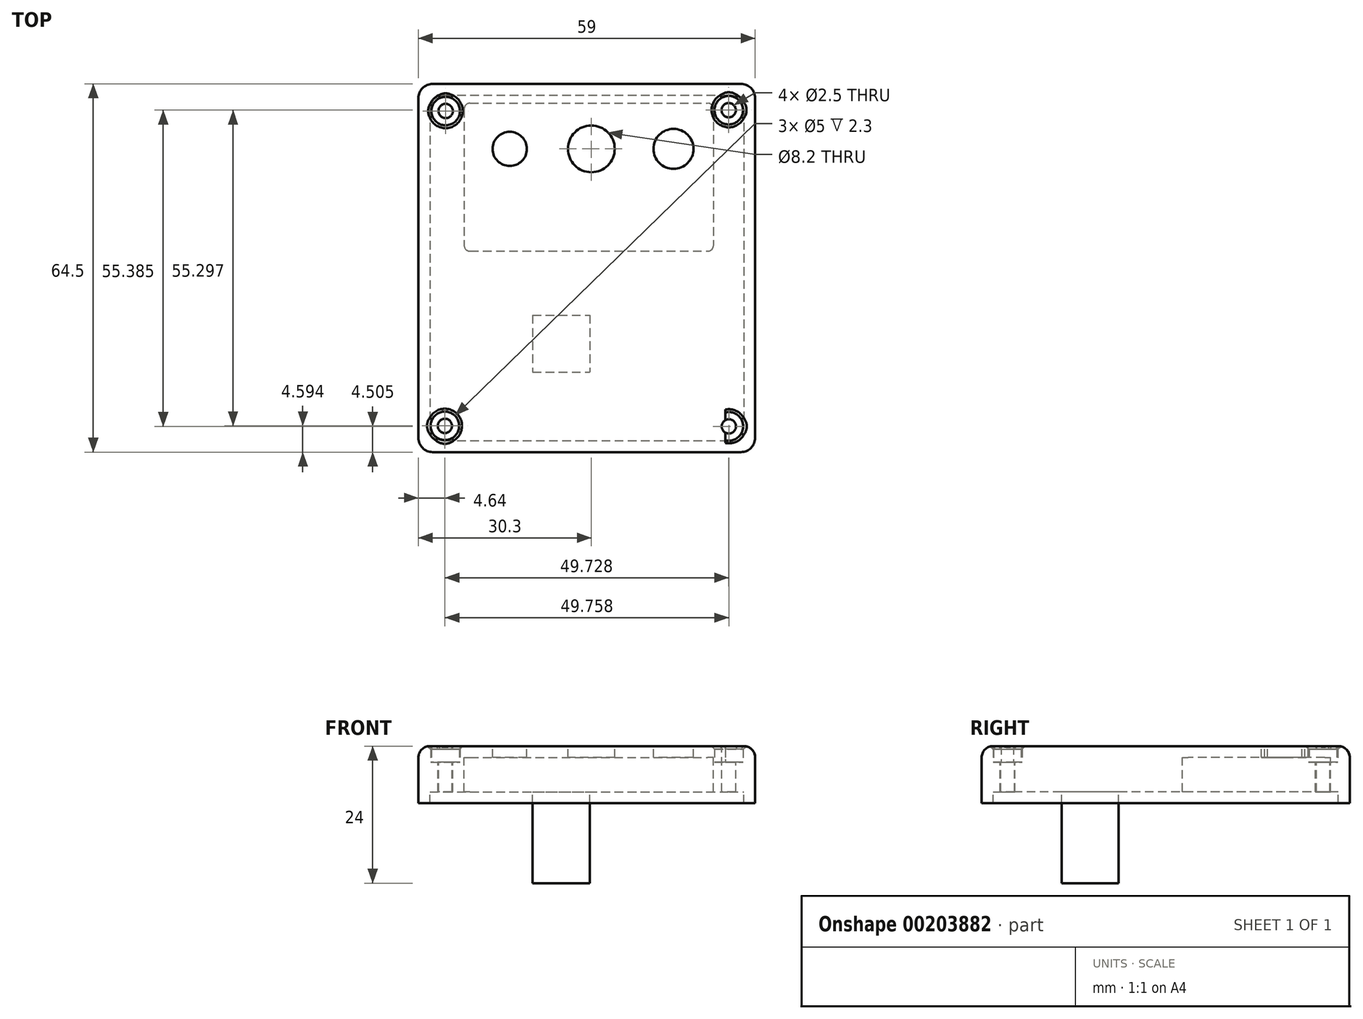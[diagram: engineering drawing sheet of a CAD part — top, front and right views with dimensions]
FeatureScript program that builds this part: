
annotation { "Feature Type Name" : "Feature", "Feature Type Description" : "" }
export const myFeature = defineFeature(function(context is Context, id is Id, definition is map)
    precondition{}
    {
        {
            var Q0;
            Q0=qCreatedBy(makeId("Top.planeOp"),FACE);
            var sketch = newSketch(context, id + "F0", { "sketchPlane" : qUnion([Q0])});
            skLineSegment(sketch, "E0.bottom", {"start": v(-36.58, 47.75) * mm, "end": v(22.42, 47.75) * mm});
            skLineSegment(sketch, "E0.top", {"start": v(-36.58, -16.75) * mm, "end": v(22.42, -16.75) * mm});
            skLineSegment(sketch, "E0.left", {"start": v(-36.58, 47.75) * mm, "end": v(-36.58, -16.75) * mm});
            skLineSegment(sketch, "E0.right", {"start": v(22.42, 47.75) * mm, "end": v(22.42, -16.75) * mm});
            skLineSegment(sketch, "E1.bottom", {"start": v(-34.58, 45.75) * mm, "end": v(20.42, 45.75) * mm});
            skLineSegment(sketch, "E1.top", {"start": v(-34.58, -14.75) * mm, "end": v(20.42, -14.75) * mm});
            skLineSegment(sketch, "E1.left", {"start": v(-34.58, 45.75) * mm, "end": v(-34.58, -14.75) * mm});
            skLineSegment(sketch, "E1.right", {"start": v(20.42, 45.75) * mm, "end": v(20.42, -14.75) * mm});
            skLineSegment(sketch, "E2.right", {"start": v(-34.58, -2) * mm, "end": v(-34.58, 2) * mm});
            skLineSegment(sketch, "E3.bottom", {"start": v(-34.58, 45.75) * mm, "end": v(9.72, 45.75) * mm});
            skLineSegment(sketch, "E4.top", {"start": v(-34.58, -14.75) * mm, "end": v(-32.58, -14.75) * mm});
            skLineSegment(sketch, "E4.left", {"start": v(-34.58, -8.75) * mm, "end": v(-34.58, -14.75) * mm});
            skLineSegment(sketch, "E5.bottom", {"start": v(13.36, 45.75) * mm, "end": v(14.86, 45.75) * mm});
            skLineSegment(sketch, "E6.top", {"start": v(16.3, -14.75) * mm, "end": v(14.92, -14.75) * mm});
            skLineSegment(sketch, "E7.bottom", {"start": v(17.21, 9.77) * mm, "end": v(11.21, 9.77) * mm});
            skLineSegment(sketch, "E7.top", {"start": v(17.21, 4.77) * mm, "end": v(11.21, 4.77) * mm});
            skLineSegment(sketch, "E7.left", {"start": v(17.21, 9.77) * mm, "end": v(17.21, 4.77) * mm});
            skLineSegment(sketch, "E7.right", {"start": v(11.21, 9.77) * mm, "end": v(11.21, 4.77) * mm});
            skCircle(sketch, "E8", {"center": v(-31.94, -12.16) * mm, "radius": 1.25 * mm});
            skCircle(sketch, "E9", {"center": v(-31.8, 43) * mm, "radius": 2.5 * mm});
            skCircle(sketch, "E10", {"center": v(-31.8, 43) * mm, "radius": 1.25 * mm});
            skLineSegment(sketch, "E11", {"start": v(-29.3, 43) * mm, "end": v(-29.3, 45.75) * mm});
            skLineSegment(sketch, "E12.bottom", {"start": v(17.22, 16.75) * mm, "end": v(-34.58, 16.75) * mm});
            skLineSegment(sketch, "E12.top", {"start": v(17.22, 15.25) * mm, "end": v(-34.58, 15.25) * mm});
            skLineSegment(sketch, "E12.left", {"start": v(17.22, 15.25) * mm, "end": v(17.22, 16.75) * mm});
            skLineSegment(sketch, "E12.right", {"start": v(-34.58, 15.25) * mm, "end": v(-34.58, 16.75) * mm});
            skLineSegment(sketch, "E13.bottom", {"start": v(-34.58, 14.63) * mm, "end": v(-32.58, 14.63) * mm});
            skLineSegment(sketch, "E13.top", {"start": v(-34.58, 8.63) * mm, "end": v(-32.58, 8.63) * mm});
            skLineSegment(sketch, "E13.left", {"start": v(-34.58, 14.63) * mm, "end": v(-34.58, 8.63) * mm});
            skLineSegment(sketch, "E13.right", {"start": v(-32.58, 14.63) * mm, "end": v(-32.58, 8.63) * mm});
            skCircle(sketch, "E14", {"center": v(17.79, 43.14) * mm, "radius": 2.5 * mm});
            skCircle(sketch, "E15", {"center": v(17.79, 43.14) * mm, "radius": 1.25 * mm});
            skLineSegment(sketch, "E16", {"start": v(17.79, 40.64) * mm, "end": v(20.42, 40.64) * mm});
            skCircle(sketch, "E17", {"center": v(17.82, -12.24) * mm, "radius": 2.5 * mm});
            skCircle(sketch, "E18", {"center": v(17.82, -12.24) * mm, "radius": 1.25 * mm});
            skLineSegment(sketch, "E19", {"start": v(17.82, -9.74) * mm, "end": v(20.42, -9.74) * mm});
            skLineSegment(sketch, "E20.bottom", {"start": v(14.92, -14.75) * mm, "end": v(13.15, -14.75) * mm});
            skLineSegment(sketch, "E20.top", {"start": v(14.92, -13.29) * mm, "end": v(13.15, -13.29) * mm});
            skLineSegment(sketch, "E20.left", {"start": v(14.92, -14.75) * mm, "end": v(14.92, -13.29) * mm});
            skLineSegment(sketch, "E20.right", {"start": v(13.15, -14.75) * mm, "end": v(13.15, -13.29) * mm});
            skLineSegment(sketch, "E21", {"start": v(17.22, 45.75) * mm, "end": v(17.22, -14.75) * mm});
            skLineSegment(sketch, "E22", {"start": v(20.42, -9.02) * mm, "end": v(17.22, -9.02) * mm});
            skLineSegment(sketch, "E23.top", {"start": v(14.92, -7.79) * mm, "end": v(13.15, -7.79) * mm});
            skLineSegment(sketch, "E23.left", {"start": v(14.92, -13.29) * mm, "end": v(14.92, -7.79) * mm});
            skLineSegment(sketch, "E23.right", {"start": v(13.15, -13.29) * mm, "end": v(13.15, -7.79) * mm});
            skLineSegment(sketch, "E24", {"start": v(15.29, 43.14) * mm, "end": v(15.29, 45.75) * mm});
            skLineSegment(sketch, "E25", {"start": v(15.32, -12.24) * mm, "end": v(15.32, -14.75) * mm});
            skLineSegment(sketch, "E26.bottom", {"start": v(-19.58, -1.75) * mm, "end": v(5.42, -1.75) * mm});
            skLineSegment(sketch, "E26.top", {"start": v(-19.58, 7.25) * mm, "end": v(5.42, 7.25) * mm});
            skLineSegment(sketch, "E26.left", {"start": v(-19.58, -1.75) * mm, "end": v(-19.58, 7.25) * mm});
            skLineSegment(sketch, "E26.right", {"start": v(5.42, -1.75) * mm, "end": v(5.42, 7.25) * mm});
            skCircle(sketch, "E27", {"center": v(8.11, 36.36) * mm, "radius": 3.5 * mm});
            skLineSegment(sketch, "E28", {"start": v(-29.58, 15.25) * mm, "end": v(-29.58, -14.75) * mm, "construction": true});
            skLineSegment(sketch, "E29", {"start": v(17.22, 1.25) * mm, "end": v(-34.58, 1.25) * mm, "construction": true});
            skLineSegment(sketch, "E30", {"start": v(-34.58, 6.25) * mm, "end": v(17.21, 6.25) * mm, "construction": true});
            skLineSegment(sketch, "E31.right", {"start": v(8.3, -10.55) * mm, "end": v(8.3, -13.55) * mm});
            skCircle(sketch, "E32", {"center": v(-31.94, -12.16) * mm, "radius": 2.5 * mm});
            skLineSegment(sketch, "E33.bottom", {"start": v(-28.56, 44.36) * mm, "end": v(15.11, 44.36) * mm});
            skLineSegment(sketch, "E33.top", {"start": v(-28.56, 18.44) * mm, "end": v(15.11, 18.44) * mm});
            skLineSegment(sketch, "E33.left", {"start": v(-28.56, 44.36) * mm, "end": v(-28.56, 18.44) * mm});
            skLineSegment(sketch, "E33.right", {"start": v(15.11, 44.36) * mm, "end": v(15.11, 18.44) * mm});
            skLineSegment(sketch, "E34", {"start": v(-31.8, 40.5) * mm, "end": v(-34.58, 40.5) * mm});
            skLineSegment(sketch, "E35.bottom", {"start": v(-20, -2.24) * mm, "end": v(5.9, -2.24) * mm});
            skLineSegment(sketch, "E35.top", {"start": v(-20, 7.67) * mm, "end": v(5.9, 7.67) * mm});
            skLineSegment(sketch, "E35.left", {"start": v(-20, -2.24) * mm, "end": v(-20, 7.67) * mm});
            skLineSegment(sketch, "E35.right", {"start": v(5.9, -2.24) * mm, "end": v(5.9, 7.67) * mm});
            skCircle(sketch, "E36", {"center": v(-20.58, 36.36) * mm, "radius": 3 * mm});
            skPoint(sketch, "E37.oppositeSnap0", {"position": v(13.15, -10.54) * mm});
            skLineSegment(sketch, "E37.bottom", {"start": v(8.3, -13.55) * mm, "end": v(12.3, -13.55) * mm});
            skLineSegment(sketch, "E37.top", {"start": v(8.3, -10.54) * mm, "end": v(12.3, -10.54) * mm});
            skLineSegment(sketch, "E37.left", {"start": v(8.3, -13.55) * mm, "end": v(8.3, -10.54) * mm});
            skLineSegment(sketch, "E37.right", {"start": v(12.3, -13.55) * mm, "end": v(12.3, -10.54) * mm});
            skLineSegment(sketch, "E38", {"start": v(12.3, -13.55) * mm, "end": v(12.3, 17.84) * mm, "construction": true});
            skLineSegment(sketch, "E39.bottom", {"start": v(12.3, 15.25) * mm, "end": v(8.3, 15.25) * mm});
            skLineSegment(sketch, "E39.top", {"start": v(12.3, 13.25) * mm, "end": v(8.3, 13.25) * mm});
            skLineSegment(sketch, "E39.left", {"start": v(12.3, 15.25) * mm, "end": v(12.3, 13.25) * mm});
            skLineSegment(sketch, "E39.right", {"start": v(8.3, 15.25) * mm, "end": v(8.3, 13.25) * mm});
            skLineSegment(sketch, "E40", {"start": v(-6.28, 41.9) * mm, "end": v(-6.28, 32.7) * mm, "construction": true});
            skLineSegment(sketch, "E41", {"start": v(8.11, 36.36) * mm, "end": v(-21.69, 36.36) * mm, "construction": true});
            skCircle(sketch, "E42", {"center": v(-6.28, 36.36) * mm, "radius": 4.1 * mm});
            skSolve(sketch);
        }
        {
            var Q0;
            Q0=qCreatedBy(makeId("Top.planeOp"),FACE);
            var sketch = newSketch(context, id + "F1", { "sketchPlane" : qUnion([Q0])});
            skLineSegment(sketch, "E43.bottom", {"start": v(-36.58, 47.75) * mm, "end": v(22.42, 47.75) * mm});
            skLineSegment(sketch, "E43.top", {"start": v(-36.58, -16.75) * mm, "end": v(22.42, -16.75) * mm});
            skLineSegment(sketch, "E43.left", {"start": v(-36.58, 47.75) * mm, "end": v(-36.58, -16.75) * mm});
            skLineSegment(sketch, "E43.right", {"start": v(22.42, 47.75) * mm, "end": v(22.42, -16.75) * mm});
            skLineSegment(sketch, "E44.bottom", {"start": v(-34.58, 45.75) * mm, "end": v(20.42, 45.75) * mm});
            skLineSegment(sketch, "E44.top", {"start": v(-34.58, -14.75) * mm, "end": v(20.42, -14.75) * mm});
            skLineSegment(sketch, "E44.left", {"start": v(-34.58, 45.75) * mm, "end": v(-34.58, -14.75) * mm});
            skLineSegment(sketch, "E44.right", {"start": v(20.42, 45.75) * mm, "end": v(20.42, -14.75) * mm});
            skSolve(sketch);
        }
        {
            var Q0;
            Q0=qCreatedBy(makeId("Top.planeOp"),FACE);
            var sketch = newSketch(context, id + "F2", { "sketchPlane" : qUnion([Q0])});
            skLineSegment(sketch, "E45.bottom", {"start": v(-32.68, -7.56) * mm, "end": v(-26.46, -7.56) * mm});
            skLineSegment(sketch, "E45.top", {"start": v(-32.68, 10.68) * mm, "end": v(-26.46, 10.68) * mm});
            skLineSegment(sketch, "E45.left", {"start": v(-32.68, -7.56) * mm, "end": v(-32.68, 10.68) * mm});
            skLineSegment(sketch, "E45.right", {"start": v(-26.46, -7.56) * mm, "end": v(-26.46, 10.68) * mm});
            skSolve(sketch);
        }
        {
            var Q0;
            Q0=qCreatedBy(makeId("Top.planeOp"),FACE);
            var sketch = newSketch(context, id + "F3", { "sketchPlane" : qUnion([Q0])});
            skLineSegment(sketch, "E46.bottom", {"start": v(-36.58, 47.75) * mm, "end": v(22.42, 47.75) * mm});
            skLineSegment(sketch, "E46.top", {"start": v(-36.58, -16.75) * mm, "end": v(22.42, -16.75) * mm});
            skLineSegment(sketch, "E46.left", {"start": v(-36.58, 47.75) * mm, "end": v(-36.58, -16.75) * mm});
            skLineSegment(sketch, "E46.right", {"start": v(22.42, 47.75) * mm, "end": v(22.42, -16.75) * mm});
            skLineSegment(sketch, "E47", {"start": v(-29.58, 14.75) * mm, "end": v(-29.58, -29.34) * mm, "construction": true});
            skLineSegment(sketch, "E48", {"start": v(20.42, -4.25) * mm, "end": v(-34.58, -4.25) * mm, "construction": true});
            skLineSegment(sketch, "E49", {"start": v(17.22, 1.75) * mm, "end": v(-34.58, 1.75) * mm, "construction": true});
            skLineSegment(sketch, "E50", {"start": v(-34.58, 7.75) * mm, "end": v(-24.59, 7.75) * mm, "construction": true});
            skCircle(sketch, "E51", {"center": v(-29.58, -4.25) * mm, "radius": 2 * mm});
            skCircle(sketch, "E52", {"center": v(-29.58, 1.75) * mm, "radius": 2 * mm});
            skCircle(sketch, "E53", {"center": v(-29.58, 7.75) * mm, "radius": 2 * mm});
            skCircle(sketch, "E54", {"center": v(-29.58, 7.75) * mm, "radius": 2.75 * mm});
            skCircle(sketch, "E55", {"center": v(-29.58, 1.75) * mm, "radius": 2.75 * mm});
            skCircle(sketch, "E56", {"center": v(-29.58, -4.25) * mm, "radius": 2.75 * mm});
            skSolve(sketch);
        }
        {
            var Q0;
            Q0=makeQuery(id+"F1.imprint","IMPRINT",FACE,{"disambiguationData":[TD([[makeQuery(id+"F1.imprint","IMPRINT",EDGE,{"derivedFrom":sQuery(id+"F1.wireOp",EDGE,"E44.bottom")}),-1.0]])]});
            extrude(context, id + "F4", {"entities" : qUnion([Q0]), "oppositeDirection" : true, "depth" : 8 * mm});
        }
        {
            var Q0;
            Q0=makeQuery(id+"F1.imprint","IMPRINT",FACE,{"disambiguationData":[TD([[makeQuery(id+"F1.imprint","IMPRINT",EDGE,{"derivedFrom":sQuery(id+"F1.wireOp",EDGE,"E43.bottom")}),-1.0]])]});
            extrude(context, id + "F5", {"entities" : qUnion([Q0]), "operationType" : NewBodyOperationType.ADD, "oppositeDirection" : true, "depth" : 10 * mm});
        }
        {
            var Q0;
            {var subQ0=sQuery(id+"F0.wireOp",EDGE,"E8");var subQ1=sQuery(id+"F0.wireOp",EDGE,"E4.right");var subQ2=makeQuery(id+"F0.imprint","INTERSECT",VERTEX,{"disambiguationData":[OD(0.0)],"derivedFrom":[subQ1,subQ0]});Q0=makeQuery(id+"F0.imprint","IMPRINT",FACE,{"disambiguationData":[TD([[makeQuery(id+"F0.imprint","IMPRINT",EDGE,{"disambiguationData":[TD([[subQ2,-1.0]])],"derivedFrom":subQ1}),1.0]])]});}
            var Q1;
            {var subQ0=sQuery(id+"F0.wireOp",EDGE,"E8");var subQ1=sQuery(id+"F0.wireOp",EDGE,"E4.right");var subQ2=makeQuery(id+"F0.imprint","INTERSECT",VERTEX,{"disambiguationData":[OD(0.0)],"derivedFrom":[subQ1,subQ0]});Q1=makeQuery(id+"F0.imprint","IMPRINT",FACE,{"disambiguationData":[TD([[makeQuery(id+"F0.imprint","IMPRINT",EDGE,{"disambiguationData":[TD([[subQ2,-1.0]])],"derivedFrom":subQ1}),-1.0]])]});}
            var Q2;
            Q2=makeQuery(id+"F0.imprint","IMPRINT",FACE,{"disambiguationData":[TD([[makeQuery(id+"F0.imprint","IMPRINT",EDGE,{"derivedFrom":sQuery(id+"F0.wireOp",EDGE,"E10")}),1.0]])]});
            var Q3;
            {var subQ0=sQuery(id+"F0.wireOp",EDGE,"E21");var subQ1=sQuery(id+"F0.wireOp",EDGE,"E18");var subQ2=makeQuery(id+"F0.imprint","INTERSECT",VERTEX,{"disambiguationData":[OD(0.0)],"derivedFrom":[subQ1,subQ0]});Q3=makeQuery(id+"F0.imprint","IMPRINT",FACE,{"disambiguationData":[TD([[makeQuery(id+"F0.imprint","IMPRINT",EDGE,{"disambiguationData":[TD([[subQ2,1.0]])],"derivedFrom":subQ1}),1.0]])]});}
            var Q4;
            {var subQ0=sQuery(id+"F0.wireOp",EDGE,"E21");var subQ1=sQuery(id+"F0.wireOp",EDGE,"E18");var subQ2=makeQuery(id+"F0.imprint","INTERSECT",VERTEX,{"disambiguationData":[OD(0.0)],"derivedFrom":[subQ1,subQ0]});Q4=makeQuery(id+"F0.imprint","IMPRINT",FACE,{"disambiguationData":[TD([[makeQuery(id+"F0.imprint","IMPRINT",EDGE,{"disambiguationData":[TD([[subQ2,-1.0]])],"derivedFrom":subQ1}),1.0]])]});}
            var Q5;
            Q5=makeQuery(id+"F0.imprint","IMPRINT",FACE,{"disambiguationData":[TD([[makeQuery(id+"F0.imprint","IMPRINT",EDGE,{"derivedFrom":sQuery(id+"F0.wireOp",EDGE,"E27")}),1.0]])]});
            var Q6;
            {var subQ0=sQuery(id+"F0.wireOp",EDGE,"E21");var subQ1=sQuery(id+"F0.wireOp",EDGE,"E15");var subQ2=makeQuery(id+"F0.imprint","INTERSECT",VERTEX,{"disambiguationData":[OD(0.0)],"derivedFrom":[subQ1,subQ0]});Q6=makeQuery(id+"F0.imprint","IMPRINT",FACE,{"disambiguationData":[TD([[makeQuery(id+"F0.imprint","IMPRINT",EDGE,{"disambiguationData":[TD([[subQ2,1.0]])],"derivedFrom":subQ1}),1.0]])]});}
            var Q7;
            {var subQ0=sQuery(id+"F0.wireOp",EDGE,"E21");var subQ1=sQuery(id+"F0.wireOp",EDGE,"E15");var subQ2=makeQuery(id+"F0.imprint","INTERSECT",VERTEX,{"disambiguationData":[OD(0.0)],"derivedFrom":[subQ1,subQ0]});Q7=makeQuery(id+"F0.imprint","IMPRINT",FACE,{"disambiguationData":[TD([[makeQuery(id+"F0.imprint","IMPRINT",EDGE,{"disambiguationData":[TD([[subQ2,-1.0]])],"derivedFrom":subQ1}),1.0]])]});}
            var Q8;
            Q8=makeQuery(id+"F0.imprint","IMPRINT",FACE,{"disambiguationData":[TD([[makeQuery(id+"F0.imprint","IMPRINT",EDGE,{"derivedFrom":sQuery(id+"F0.wireOp",EDGE,"E8")}),1.0]])]});
            extrude(context, id + "F6", {"entities" : qUnion([Q0, Q1, Q2, Q3, Q4, Q5, Q6, Q7, Q8]), "operationType" : NewBodyOperationType.REMOVE, "oppositeDirection" : true, "depth" : 9.6 * mm});
        }
        {
            var Q0;
            Q0=makeQuery(id+"F2.imprint","IMPRINT",FACE,{"disambiguationData":[TD([[makeQuery(id+"F2.imprint","IMPRINT",EDGE,{"derivedFrom":sQuery(id+"F2.wireOp",EDGE,"E45.bottom")}),1.0]])]});
            extrude(context, id + "F7", {"entities" : qUnion([Q0]), "operationType" : NewBodyOperationType.ADD, "oppositeDirection" : true, "depth" : 4.07 * mm});
        }
        {
            var Q0;
            Q0=makeQuery(id+"F5.opExtrude","SWEPT_EDGE",EDGE,{"disambiguationData":[OSD([sQuery(id+"F1.wireOp",EDGE,"E43.top"),sQuery(id+"F1.wireOp",EDGE,"E43.right")])]});
            var Q1;
            Q1=makeQuery(id+"F5.opExtrude","SWEPT_EDGE",EDGE,{"disambiguationData":[OSD([sQuery(id+"F1.wireOp",EDGE,"E43.bottom"),sQuery(id+"F1.wireOp",EDGE,"E43.right")])]});
            var Q2;
            Q2=makeQuery(id+"F5.opExtrude","SWEPT_EDGE",EDGE,{"disambiguationData":[OSD([sQuery(id+"F1.wireOp",EDGE,"E43.top"),sQuery(id+"F1.wireOp",EDGE,"E43.left")])]});
            var Q3;
            Q3=makeQuery(id+"F5.opExtrude","SWEPT_EDGE",EDGE,{"disambiguationData":[OSD([sQuery(id+"F1.wireOp",EDGE,"E43.bottom"),sQuery(id+"F1.wireOp",EDGE,"E43.left")])]});
            fillet(context, id + "F8", {"entities" : qUnion([Q0, Q1, Q2, Q3]), "radius" : 2.5 * mm, "tangentPropagation" : true, "allowEdgeOverflow" : false});
        }
        {
            var Q0;
            Q0=makeQuery(id+"F0.imprint","IMPRINT",FACE,{"disambiguationData":[TD([[makeQuery(id+"F0.imprint","IMPRINT",EDGE,{"derivedFrom":sQuery(id+"F0.wireOp",EDGE,"E27")}),-1.0]])]});
            extrude(context, id + "F9", {"entities" : qUnion([Q0]), "operationType" : NewBodyOperationType.REMOVE, "oppositeDirection" : true, "depth" : 25 * mm, "hasSecondDirection" : true, "secondDirectionOppositeDirection" : true, "secondDirectionDepth" : 2 * mm});
        }
        {
            var Q0;
            {var subQ4=sQuery(id+"F0.wireOp",EDGE,"E17");var subQ5=makeQuery(id+"F0.imprint","INTERSECT",VERTEX,{"derivedFrom":[subQ4,sQuery(id+"F0.wireOp",EDGE,"E25")]});Q0=makeQuery(id+"F0.imprint","IMPRINT",FACE,{"disambiguationData":[TD([[makeQuery(id+"F0.imprint","IMPRINT",EDGE,{"disambiguationData":[TD([[subQ5,1.0]])],"derivedFrom":subQ4}),1.0]])]});}
            var Q1;
            {var subQ1=sQuery(id+"F0.wireOp",EDGE,"E17");var subQ6=makeQuery(id+"F0.imprint","INTERSECT",VERTEX,{"derivedFrom":[subQ1,sQuery(id+"F0.wireOp",EDGE,"E19")]});Q1=makeQuery(id+"F0.imprint","IMPRINT",FACE,{"disambiguationData":[TD([[makeQuery(id+"F0.imprint","IMPRINT",EDGE,{"disambiguationData":[TD([[subQ6,-1.0]])],"derivedFrom":subQ1}),1.0]])]});}
            var Q2;
            Q2=makeQuery(id+"F0.imprint","IMPRINT",FACE,{"disambiguationData":[TD([[makeQuery(id+"F0.imprint","IMPRINT",EDGE,{"derivedFrom":sQuery(id+"F0.wireOp",EDGE,"E10")}),-1.0]])]});
            var Q3;
            {var subQ0=sQuery(id+"F0.wireOp",EDGE,"PLKqhVFR-8eKu-Ixv1-GPgQ-gXaM0qRD25Is");var subQ2=sQuery(id+"F0.wireOp",EDGE,"E4.right");var subQ7=makeQuery(id+"F0.imprint","INTERSECT",VERTEX,{"disambiguationData":[OD(0.0)],"derivedFrom":[subQ2,subQ0]});Q3=makeQuery(id+"F0.imprint","IMPRINT",FACE,{"disambiguationData":[TD([[makeQuery(id+"F0.imprint","IMPRINT",EDGE,{"disambiguationData":[TD([[subQ7,-1.0]])],"derivedFrom":subQ2}),1.0]])]});}
            var Q4;
            {var subQ0=sQuery(id+"F0.wireOp",EDGE,"PLKqhVFR-8eKu-Ixv1-GPgQ-gXaM0qRD25Is");var subQ1=sQuery(id+"F0.wireOp",EDGE,"E4.right");var subQ2=makeQuery(id+"F0.imprint","INTERSECT",VERTEX,{"disambiguationData":[OD(0.0)],"derivedFrom":[subQ1,subQ0]});Q4=makeQuery(id+"F0.imprint","IMPRINT",FACE,{"disambiguationData":[TD([[makeQuery(id+"F0.imprint","IMPRINT",EDGE,{"disambiguationData":[TD([[subQ2,-1.0]])],"derivedFrom":subQ1}),-1.0]])]});}
            var Q5;
            {var subQ1=sQuery(id+"F0.wireOp",EDGE,"E14");var subQ6=makeQuery(id+"F0.imprint","INTERSECT",VERTEX,{"derivedFrom":[subQ1,sQuery(id+"F0.wireOp",EDGE,"E24")]});Q5=makeQuery(id+"F0.imprint","IMPRINT",FACE,{"disambiguationData":[TD([[makeQuery(id+"F0.imprint","IMPRINT",EDGE,{"disambiguationData":[TD([[subQ6,1.0]])],"derivedFrom":subQ1}),1.0]])]});}
            var Q6;
            {var subQ4=sQuery(id+"F0.wireOp",EDGE,"E14");var subQ6=makeQuery(id+"F0.imprint","INTERSECT",VERTEX,{"derivedFrom":[subQ4,sQuery(id+"F0.wireOp",EDGE,"E16")]});Q6=makeQuery(id+"F0.imprint","IMPRINT",FACE,{"disambiguationData":[TD([[makeQuery(id+"F0.imprint","IMPRINT",EDGE,{"disambiguationData":[TD([[subQ6,1.0]])],"derivedFrom":subQ4}),1.0]])]});}
            var Q7;
            {var subQ3=sQuery(id+"F0.wireOp",EDGE,"E32");var subQ5=sQuery(id+"F0.wireOp",EDGE,"E4.right");var subQ6=makeQuery(id+"F0.imprint","INTERSECT",VERTEX,{"disambiguationData":[OD(0.0)],"derivedFrom":[subQ5,subQ3]});Q7=makeQuery(id+"F0.imprint","IMPRINT",FACE,{"disambiguationData":[TD([[makeQuery(id+"F0.imprint","IMPRINT",EDGE,{"disambiguationData":[TD([[subQ6,-1.0]])],"derivedFrom":subQ5}),1.0]])]});}
            var Q8;
            {var subQ1=sQuery(id+"F0.wireOp",EDGE,"E4.right");var subQ6=sQuery(id+"F0.wireOp",EDGE,"kjhwjDdY-w9so-hjMB-xEs9-QlES4Zc8QczL");var subQ7=makeQuery(id+"F0.imprint","INTERSECT",VERTEX,{"derivedFrom":[subQ1,subQ6]});Q8=makeQuery(id+"F0.imprint","IMPRINT",FACE,{"disambiguationData":[TD([[makeQuery(id+"F0.imprint","IMPRINT",EDGE,{"disambiguationData":[TD([[subQ7,-1.0]])],"derivedFrom":subQ1}),-1.0]])]});}
            var Q9;
            {var subQ0=sQuery(id+"F0.wireOp",EDGE,"E32");var subQ1=sQuery(id+"F0.wireOp",EDGE,"E4.right");var subQ2=makeQuery(id+"F0.imprint","INTERSECT",VERTEX,{"disambiguationData":[OD(0.0)],"derivedFrom":[subQ1,subQ0]});Q9=makeQuery(id+"F0.imprint","IMPRINT",FACE,{"disambiguationData":[TD([[makeQuery(id+"F0.imprint","IMPRINT",EDGE,{"disambiguationData":[TD([[subQ2,-1.0]])],"derivedFrom":subQ1}),-1.0]])]});}
            var Q10;
            Q10=makeQuery(id+"F0.imprint","IMPRINT",FACE,{"disambiguationData":[TD([[makeQuery(id+"F0.imprint","IMPRINT",EDGE,{"derivedFrom":sQuery(id+"F0.wireOp",EDGE,"E8")}),-1.0]])]});
            extrude(context, id + "F10", {"entities" : qUnion([Q0, Q1, Q2, Q3, Q4, Q5, Q6, Q7, Q8, Q9, Q10]), "operationType" : NewBodyOperationType.REMOVE, "depth" : 3.9 * mm, "hasSecondDirection" : true, "secondDirectionOppositeDirection" : true, "secondDirectionDepth" : 2.8 * mm});
        }
        {
            var Q0;
            Q0=makeQuery(id+"F0.imprint","IMPRINT",FACE,{"disambiguationData":[TD([[makeQuery(id+"F0.imprint","IMPRINT",EDGE,{"derivedFrom":sQuery(id+"F0.wireOp",EDGE,"EeBKnc5o-wB0O-0N6T-5B69-5pySvWSWUYzF")}),-1.0]])]});
            var Q1;
            Q1=makeQuery(id+"F0.imprint","IMPRINT",FACE,{"disambiguationData":[TD([[makeQuery(id+"F0.imprint","IMPRINT",EDGE,{"derivedFrom":sQuery(id+"F0.wireOp",EDGE,"E27")}),-1.0]])]});
            extrude(context, id + "F11", {"entities" : qUnion([Q0, Q1]), "operationType" : NewBodyOperationType.REMOVE, "oppositeDirection" : true, "depth" : 15 * mm, "hasSecondDirection" : true, "secondDirectionOppositeDirection" : true, "secondDirectionDepth" : 2 * mm});
        }
        {
            var Q0;
            Q0=makeQuery(id+"F9.boolean.opBoolean","COPY",EDGE,{"derivedFrom":makeQuery(id+"F9.opExtrude","SWEPT_EDGE",EDGE,{"disambiguationData":[OSD([sQuery(id+"F0.wireOp",EDGE,"E33.bottom"),sQuery(id+"F0.wireOp",EDGE,"E33.left")])]})});
            var Q1;
            Q1=makeQuery(id+"F9.boolean.opBoolean","COPY",EDGE,{"derivedFrom":makeQuery(id+"F9.opExtrude","SWEPT_EDGE",EDGE,{"disambiguationData":[OSD([sQuery(id+"F0.wireOp",EDGE,"E33.top"),sQuery(id+"F0.wireOp",EDGE,"E33.left")])]})});
            var Q2;
            Q2=makeQuery(id+"F9.boolean.opBoolean","COPY",EDGE,{"derivedFrom":makeQuery(id+"F9.opExtrude","SWEPT_EDGE",EDGE,{"disambiguationData":[OSD([sQuery(id+"F0.wireOp",EDGE,"E33.top"),sQuery(id+"F0.wireOp",EDGE,"E33.right")])]})});
            var Q3;
            Q3=makeQuery(id+"F9.boolean.opBoolean","COPY",EDGE,{"derivedFrom":makeQuery(id+"F9.opExtrude","SWEPT_EDGE",EDGE,{"disambiguationData":[OSD([sQuery(id+"F0.wireOp",EDGE,"E33.bottom"),sQuery(id+"F0.wireOp",EDGE,"E33.right")])]})});
            fillet(context, id + "F12", {"entities" : qUnion([Q0, Q1, Q2, Q3]), "radius" : 1 * mm, "tangentPropagation" : true, "allowEdgeOverflow" : false});
        }
        {
            var Q0;
            Q0=makeQuery(id+"F5.opExtrude","CAP_EDGE",EDGE,{"disambiguationData":[OSD([sQuery(id+"F1.wireOp",EDGE,"E43.bottom")])],"isStart":true});
            fillet(context, id + "F13", {"entities" : qUnion([Q0]), "radius" : 2 * mm, "tangentPropagation" : true, "allowEdgeOverflow" : false});
        }
        {
            var Q0;
            Q0=makeQuery(id+"F0.imprint","IMPRINT",FACE,{"disambiguationData":[TD([[makeQuery(id+"F0.imprint","IMPRINT",EDGE,{"derivedFrom":sQuery(id+"F0.wireOp",EDGE,"E36")}),1.0]])]});
            var Q1;
            Q1=makeQuery(id+"F0.imprint","IMPRINT",FACE,{"disambiguationData":[TD([[makeQuery(id+"F0.imprint","IMPRINT",EDGE,{"derivedFrom":sQuery(id+"F0.wireOp",EDGE,"E42")}),1.0]])]});
            extrude(context, id + "F14", {"entities" : qUnion([Q0, Q1]), "operationType" : NewBodyOperationType.REMOVE, "oppositeDirection" : true, "depth" : 25 * mm});
        }
        {
            var Q0;
            Q0=qCreatedBy(makeId("Top.planeOp"),FACE);
            var sketch = newSketch(context, id + "F15", { "sketchPlane" : qUnion([Q0])});
            skLineSegment(sketch, "E57.bottom", {"start": v(-16.58, 7.25) * mm, "end": v(-6.58, 7.25) * mm});
            skLineSegment(sketch, "E57.top", {"start": v(-16.58, -2.75) * mm, "end": v(-6.58, -2.75) * mm});
            skLineSegment(sketch, "E57.left", {"start": v(-16.58, 7.25) * mm, "end": v(-16.58, -2.75) * mm});
            skLineSegment(sketch, "E57.right", {"start": v(-6.58, 7.25) * mm, "end": v(-6.58, -2.75) * mm});
            skSolve(sketch);
        }
        {
            var Q0;
            Q0 = qSketchRegion(id + "F15", true);
            extrude(context, id + "F16", {"entities" : qUnion([Q0]), "oppositeDirection" : true, "depth" : 24 * mm, "hasSecondDirection" : true, "secondDirectionOppositeDirection" : true, "secondDirectionDepth" : 8 * mm});
        }
        {
            var Q0;
            {var subQ0=sQuery(id+"F1.wireOp",EDGE,"E44.right");var subQ1=sQuery(id+"F1.wireOp",EDGE,"E44.left");var subQ2=sQuery(id+"F1.wireOp",EDGE,"E44.top");var subQ3=sQuery(id+"F1.wireOp",EDGE,"E44.bottom");Q0=makeQuery(id+"F10.boolean.opBoolean","INTERSECT",EDGE,{"derivedFrom":[makeQuery(id+"F5.boolean.opBoolean","MERGE",FACE,{"derivedFrom":[makeQuery(id+"F4.opExtrude","CAP_FACE",FACE,{"disambiguationData":[OSD([subQ3,subQ2,subQ1,subQ0])],"isStart":true}),makeQuery(id+"F5.opExtrude","CAP_FACE",FACE,{"disambiguationData":[OSD([sQuery(id+"F1.wireOp",EDGE,"E43.bottom"),sQuery(id+"F1.wireOp",EDGE,"E43.top"),sQuery(id+"F1.wireOp",EDGE,"E43.left"),sQuery(id+"F1.wireOp",EDGE,"E43.right"),subQ3,subQ2,subQ1,subQ0])],"isStart":true})]}),makeQuery(id+"F10.opExtrude","SWEPT_FACE",FACE,{"disambiguationData":[OSD([sQuery(id+"F0.wireOp",EDGE,"E9")])]})]});}
            var Q1;
            {var subQ0=sQuery(id+"F1.wireOp",EDGE,"E44.right");var subQ1=sQuery(id+"F1.wireOp",EDGE,"E44.left");var subQ2=sQuery(id+"F1.wireOp",EDGE,"E44.top");var subQ3=sQuery(id+"F1.wireOp",EDGE,"E44.bottom");Q1=makeQuery(id+"F10.boolean.opBoolean","INTERSECT",EDGE,{"derivedFrom":[makeQuery(id+"F5.boolean.opBoolean","MERGE",FACE,{"derivedFrom":[makeQuery(id+"F4.opExtrude","CAP_FACE",FACE,{"disambiguationData":[OSD([subQ3,subQ2,subQ1,subQ0])],"isStart":true}),makeQuery(id+"F5.opExtrude","CAP_FACE",FACE,{"disambiguationData":[OSD([sQuery(id+"F1.wireOp",EDGE,"E43.bottom"),sQuery(id+"F1.wireOp",EDGE,"E43.top"),sQuery(id+"F1.wireOp",EDGE,"E43.left"),sQuery(id+"F1.wireOp",EDGE,"E43.right"),subQ3,subQ2,subQ1,subQ0])],"isStart":true})]}),makeQuery(id+"F10.opExtrude","SWEPT_FACE",FACE,{"disambiguationData":[OSD([sQuery(id+"F0.wireOp",EDGE,"E14")])]})]});}
            var Q2;
            {var subQ0=sQuery(id+"F1.wireOp",EDGE,"E44.right");var subQ1=sQuery(id+"F1.wireOp",EDGE,"E44.left");var subQ2=sQuery(id+"F1.wireOp",EDGE,"E44.top");var subQ3=sQuery(id+"F1.wireOp",EDGE,"E44.bottom");Q2=makeQuery(id+"F10.boolean.opBoolean","INTERSECT",EDGE,{"derivedFrom":[makeQuery(id+"F5.boolean.opBoolean","MERGE",FACE,{"derivedFrom":[makeQuery(id+"F4.opExtrude","CAP_FACE",FACE,{"disambiguationData":[OSD([subQ3,subQ2,subQ1,subQ0])],"isStart":true}),makeQuery(id+"F5.opExtrude","CAP_FACE",FACE,{"disambiguationData":[OSD([sQuery(id+"F1.wireOp",EDGE,"E43.bottom"),sQuery(id+"F1.wireOp",EDGE,"E43.top"),sQuery(id+"F1.wireOp",EDGE,"E43.left"),sQuery(id+"F1.wireOp",EDGE,"E43.right"),subQ3,subQ2,subQ1,subQ0])],"isStart":true})]}),makeQuery(id+"F10.opExtrude","SWEPT_FACE",FACE,{"disambiguationData":[OSD([sQuery(id+"F0.wireOp",EDGE,"E17")])]})]});}
            var Q3;
            {var subQ0=sQuery(id+"F1.wireOp",EDGE,"E44.right");var subQ1=sQuery(id+"F1.wireOp",EDGE,"E44.left");var subQ2=sQuery(id+"F1.wireOp",EDGE,"E44.top");var subQ3=sQuery(id+"F1.wireOp",EDGE,"E44.bottom");Q3=makeQuery(id+"F10.boolean.opBoolean","INTERSECT",EDGE,{"derivedFrom":[makeQuery(id+"F5.boolean.opBoolean","MERGE",FACE,{"derivedFrom":[makeQuery(id+"F4.opExtrude","CAP_FACE",FACE,{"disambiguationData":[OSD([subQ3,subQ2,subQ1,subQ0])],"isStart":true}),makeQuery(id+"F5.opExtrude","CAP_FACE",FACE,{"disambiguationData":[OSD([sQuery(id+"F1.wireOp",EDGE,"E43.bottom"),sQuery(id+"F1.wireOp",EDGE,"E43.top"),sQuery(id+"F1.wireOp",EDGE,"E43.left"),sQuery(id+"F1.wireOp",EDGE,"E43.right"),subQ3,subQ2,subQ1,subQ0])],"isStart":true})]}),makeQuery(id+"F10.opExtrude","SWEPT_FACE",FACE,{"disambiguationData":[OSD([sQuery(id+"F0.wireOp",EDGE,"E32")])]})]});}
            chamfer(context, id + "F17", {"entities" : qUnion([Q0, Q1, Q2, Q3]), "width" : .5 * mm, "tangentPropagation" : true});
        }
        {
            var Q0;
            Q0=makeQuery(id+"F5.opExtrude","SWEPT_EDGE",EDGE,{"disambiguationData":[OSD([sQuery(id+"F1.wireOp",EDGE,"E44.bottom"),sQuery(id+"F1.wireOp",EDGE,"E44.right")])]});
            var Q1;
            Q1=makeQuery(id+"F5.opExtrude","SWEPT_EDGE",EDGE,{"disambiguationData":[OSD([sQuery(id+"F1.wireOp",EDGE,"E44.bottom"),sQuery(id+"F1.wireOp",EDGE,"E44.left")])]});
            var Q2;
            Q2=makeQuery(id+"F5.opExtrude","SWEPT_EDGE",EDGE,{"disambiguationData":[OSD([sQuery(id+"F1.wireOp",EDGE,"E44.top"),sQuery(id+"F1.wireOp",EDGE,"E44.left")])]});
            var Q3;
            Q3=makeQuery(id+"F5.opExtrude","SWEPT_EDGE",EDGE,{"disambiguationData":[OSD([sQuery(id+"F1.wireOp",EDGE,"E44.top"),sQuery(id+"F1.wireOp",EDGE,"E44.right")])]});
            fillet(context, id + "F18", {"entities" : qUnion([Q0, Q1, Q2, Q3]), "radius" : 2.5 * mm, "tangentPropagation" : true, "allowEdgeOverflow" : false});
        }
    });
